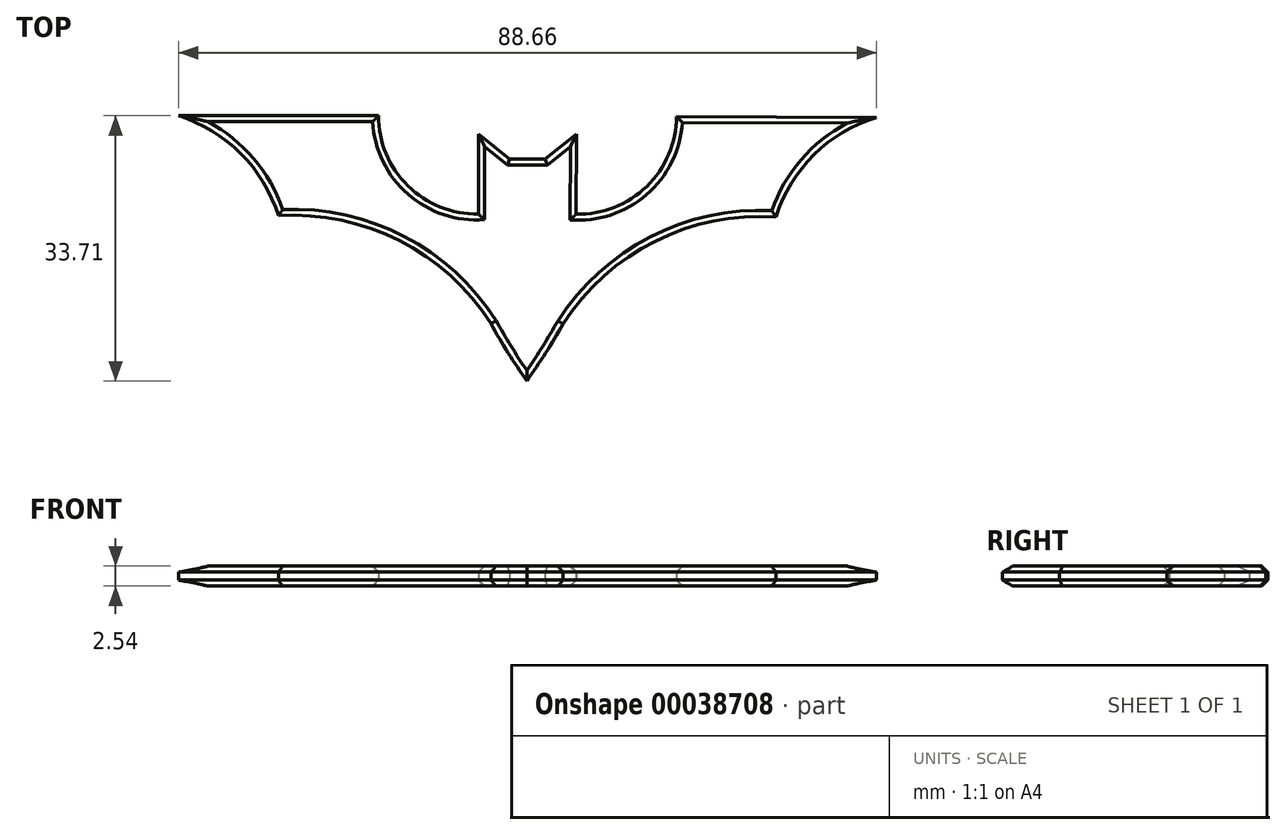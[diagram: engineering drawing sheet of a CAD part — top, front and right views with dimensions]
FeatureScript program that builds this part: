
annotation { "Feature Type Name" : "Feature", "Feature Type Description" : "" }
export const myFeature = defineFeature(function(context is Context, id is Id, definition is map)
    precondition{}
    {
        {
            var Q0;
            Q0=qCreatedBy(makeId("Top.planeOp"),FACE);
            var sketch = newSketch(context, id + "F0", { "sketchPlane" : qUnion([Q0])});
            skArc(sketch, "E0", {"start": v(-34.56, -2.44) * mm, "mid": v(-30.83, -11.33) * mm, "end": v(-21.87, -14.9) * mm});
            skLineSegment(sketch, "E1", {"start": v(-21.87, -14.9) * mm, "end": v(-21.87, -4.75) * mm});
            skLineSegment(sketch, "E2", {"start": v(-21.87, -4.75) * mm, "end": v(-17.9, -7.93) * mm});
            skLineSegment(sketch, "E3", {"start": v(-17.9, -7.93) * mm, "end": v(-15.62, -7.93) * mm});
            skLineSegment(sketch, "E4", {"start": v(-34.56, -2.44) * mm, "end": v(-59.96, -2.44) * mm});
            skArc(sketch, "E5", {"start": v(-47.26, -15.13) * mm, "mid": v(-52.04, -7.22) * mm, "end": v(-59.96, -2.44) * mm});
            skArc(sketch, "E6", {"start": v(-20.27, -28.86) * mm, "mid": v(-31.9, -18.31) * mm, "end": v(-47.26, -15.13) * mm});
            skArc(sketch, "E7", {"start": v(-20.27, -28.86) * mm, "mid": v(-18.08, -32.56) * mm, "end": v(-15.7, -36.15) * mm});
            skLineSegment(sketch, "E8.MirrorCS", {"start": v(-9.4, -4.78) * mm, "end": v(-13.37, -7.94) * mm});
            skLineSegment(sketch, "E9.MirrorCS", {"start": v(-13.37, -7.94) * mm, "end": v(-15.66, -7.93) * mm});
            skArc(sketch, "E10.MirrorCS", {"start": v(-11.1, -28.88) * mm, "mid": v(0.56, -18.39) * mm, "end": v(15.94, -15.28) * mm});
            skArc(sketch, "E11.MirrorCS", {"start": v(-11.1, -28.88) * mm, "mid": v(-13.32, -32.57) * mm, "end": v(-15.7, -36.15) * mm});
            skArc(sketch, "E12.MirrorCS", {"start": v(15.94, -15.28) * mm, "mid": v(20.77, -7.4) * mm, "end": v(28.7, -2.65) * mm});
            skLineSegment(sketch, "E13.MirrorCS", {"start": v(3.3, -2.53) * mm, "end": v(28.7, -2.65) * mm});
            skArc(sketch, "E14.MirrorCS", {"start": v(3.3, -2.53) * mm, "mid": v(-0.47, -11.4) * mm, "end": v(-9.45, -14.94) * mm});
            skLineSegment(sketch, "E15.MirrorCS", {"start": v(-9.45, -14.94) * mm, "end": v(-9.4, -4.78) * mm});
            skSolve(sketch);
        }
        {
            var Q0;
            Q0=makeQuery(id+"F0.imprint","IMPRINT",FACE,{"disambiguationData":[TD([[makeQuery(id+"F0.imprint","IMPRINT",EDGE,{"derivedFrom":sQuery(id+"F0.wireOp",EDGE,"E0")}),-1.0]])]});
            extrude(context, id + "F1", {"entities" : qUnion([Q0]), "depth" : 2.54 * mm});
        }
        {
            var Q0;
            Q0=makeQuery(id+"F1.opExtrude","CAP_EDGE",EDGE,{"disambiguationData":[OSD([sQuery(id+"F0.wireOp",EDGE,"E5")])],"isStart":false});
            var Q1;
            Q1=makeQuery(id+"F1.opExtrude","CAP_EDGE",EDGE,{"disambiguationData":[OSD([sQuery(id+"F0.wireOp",EDGE,"E4")])],"isStart":false});
            var Q2;
            Q2=makeQuery(id+"F1.opExtrude","CAP_EDGE",EDGE,{"disambiguationData":[OSD([sQuery(id+"F0.wireOp",EDGE,"E0")])],"isStart":false});
            var Q3;
            Q3=makeQuery(id+"F1.opExtrude","CAP_EDGE",EDGE,{"disambiguationData":[OSD([sQuery(id+"F0.wireOp",EDGE,"E1")])],"isStart":false});
            var Q4;
            Q4=makeQuery(id+"F1.opExtrude","CAP_EDGE",EDGE,{"disambiguationData":[OSD([sQuery(id+"F0.wireOp",EDGE,"E2")])],"isStart":false});
            var Q5;
            Q5=makeQuery(id+"F1.opExtrude","CAP_EDGE",EDGE,{"disambiguationData":[OSD([sQuery(id+"F0.wireOp",EDGE,"E3")])],"isStart":false});
            var Q6;
            Q6=makeQuery(id+"F1.opExtrude","CAP_EDGE",EDGE,{"disambiguationData":[OSD([sQuery(id+"F0.wireOp",EDGE,"E9.MirrorCS")])],"isStart":false});
            var Q7;
            Q7=makeQuery(id+"F1.opExtrude","CAP_EDGE",EDGE,{"disambiguationData":[OSD([sQuery(id+"F0.wireOp",EDGE,"E8.MirrorCS")])],"isStart":false});
            var Q8;
            Q8=makeQuery(id+"F1.opExtrude","CAP_EDGE",EDGE,{"disambiguationData":[OSD([sQuery(id+"F0.wireOp",EDGE,"E15.MirrorCS")])],"isStart":false});
            var Q9;
            Q9=makeQuery(id+"F1.opExtrude","CAP_EDGE",EDGE,{"disambiguationData":[OSD([sQuery(id+"F0.wireOp",EDGE,"E14.MirrorCS")])],"isStart":false});
            var Q10;
            Q10=makeQuery(id+"F1.opExtrude","CAP_EDGE",EDGE,{"disambiguationData":[OSD([sQuery(id+"F0.wireOp",EDGE,"E13.MirrorCS")])],"isStart":false});
            var Q11;
            Q11=makeQuery(id+"F1.opExtrude","CAP_EDGE",EDGE,{"disambiguationData":[OSD([sQuery(id+"F0.wireOp",EDGE,"E12.MirrorCS")])],"isStart":false});
            var Q12;
            Q12=makeQuery(id+"F1.opExtrude","CAP_EDGE",EDGE,{"disambiguationData":[OSD([sQuery(id+"F0.wireOp",EDGE,"E10.MirrorCS")])],"isStart":false});
            var Q13;
            Q13=makeQuery(id+"F1.opExtrude","CAP_EDGE",EDGE,{"disambiguationData":[OSD([sQuery(id+"F0.wireOp",EDGE,"E11.MirrorCS")])],"isStart":false});
            var Q14;
            Q14=makeQuery(id+"F1.opExtrude","CAP_EDGE",EDGE,{"disambiguationData":[OSD([sQuery(id+"F0.wireOp",EDGE,"E7")])],"isStart":false});
            var Q15;
            Q15=makeQuery(id+"F1.opExtrude","CAP_EDGE",EDGE,{"disambiguationData":[OSD([sQuery(id+"F0.wireOp",EDGE,"E6")])],"isStart":false});
            chamfer(context, id + "F2", {"entities" : qUnion([Q0, Q1, Q2, Q3, Q4, Q5, Q6, Q7, Q8, Q9, Q10, Q11, Q12, Q13, Q14, Q15]), "width" : 0.76 * mm, "tangentPropagation" : true});
        }
        {
            var Q0;
            Q0=makeQuery(id+"F1.opExtrude","CAP_EDGE",EDGE,{"disambiguationData":[OSD([sQuery(id+"F0.wireOp",EDGE,"E13.MirrorCS")])],"isStart":true});
            var Q1;
            Q1=makeQuery(id+"F1.opExtrude","CAP_EDGE",EDGE,{"disambiguationData":[OSD([sQuery(id+"F0.wireOp",EDGE,"E14.MirrorCS")])],"isStart":true});
            var Q2;
            Q2=makeQuery(id+"F1.opExtrude","CAP_EDGE",EDGE,{"disambiguationData":[OSD([sQuery(id+"F0.wireOp",EDGE,"E12.MirrorCS")])],"isStart":true});
            var Q3;
            Q3=makeQuery(id+"F1.opExtrude","CAP_EDGE",EDGE,{"disambiguationData":[OSD([sQuery(id+"F0.wireOp",EDGE,"E10.MirrorCS")])],"isStart":true});
            var Q4;
            Q4=makeQuery(id+"F1.opExtrude","CAP_EDGE",EDGE,{"disambiguationData":[OSD([sQuery(id+"F0.wireOp",EDGE,"E6")])],"isStart":true});
            var Q5;
            Q5=makeQuery(id+"F1.opExtrude","CAP_EDGE",EDGE,{"disambiguationData":[OSD([sQuery(id+"F0.wireOp",EDGE,"E7")])],"isStart":true});
            var Q6;
            Q6=makeQuery(id+"F1.opExtrude","CAP_EDGE",EDGE,{"disambiguationData":[OSD([sQuery(id+"F0.wireOp",EDGE,"E11.MirrorCS")])],"isStart":true});
            var Q7;
            Q7=makeQuery(id+"F1.opExtrude","CAP_EDGE",EDGE,{"disambiguationData":[OSD([sQuery(id+"F0.wireOp",EDGE,"E5")])],"isStart":true});
            var Q8;
            Q8=makeQuery(id+"F1.opExtrude","CAP_EDGE",EDGE,{"disambiguationData":[OSD([sQuery(id+"F0.wireOp",EDGE,"E4")])],"isStart":true});
            var Q9;
            Q9=makeQuery(id+"F1.opExtrude","CAP_EDGE",EDGE,{"disambiguationData":[OSD([sQuery(id+"F0.wireOp",EDGE,"E0")])],"isStart":true});
            var Q10;
            Q10=makeQuery(id+"F1.opExtrude","CAP_EDGE",EDGE,{"disambiguationData":[OSD([sQuery(id+"F0.wireOp",EDGE,"E1")])],"isStart":true});
            var Q11;
            Q11=makeQuery(id+"F1.opExtrude","CAP_EDGE",EDGE,{"disambiguationData":[OSD([sQuery(id+"F0.wireOp",EDGE,"E2")])],"isStart":true});
            var Q12;
            Q12=makeQuery(id+"F1.opExtrude","CAP_EDGE",EDGE,{"disambiguationData":[OSD([sQuery(id+"F0.wireOp",EDGE,"E3")])],"isStart":true});
            var Q13;
            Q13=makeQuery(id+"F1.opExtrude","CAP_EDGE",EDGE,{"disambiguationData":[OSD([sQuery(id+"F0.wireOp",EDGE,"E9.MirrorCS")])],"isStart":true});
            var Q14;
            Q14=makeQuery(id+"F1.opExtrude","CAP_EDGE",EDGE,{"disambiguationData":[OSD([sQuery(id+"F0.wireOp",EDGE,"E8.MirrorCS")])],"isStart":true});
            var Q15;
            Q15=makeQuery(id+"F1.opExtrude","CAP_EDGE",EDGE,{"disambiguationData":[OSD([sQuery(id+"F0.wireOp",EDGE,"E15.MirrorCS")])],"isStart":true});
            chamfer(context, id + "F3", {"entities" : qUnion([Q0, Q1, Q2, Q3, Q4, Q5, Q6, Q7, Q8, Q9, Q10, Q11, Q12, Q13, Q14, Q15]), "width" : 0.76 * mm, "tangentPropagation" : true});
        }
    });
